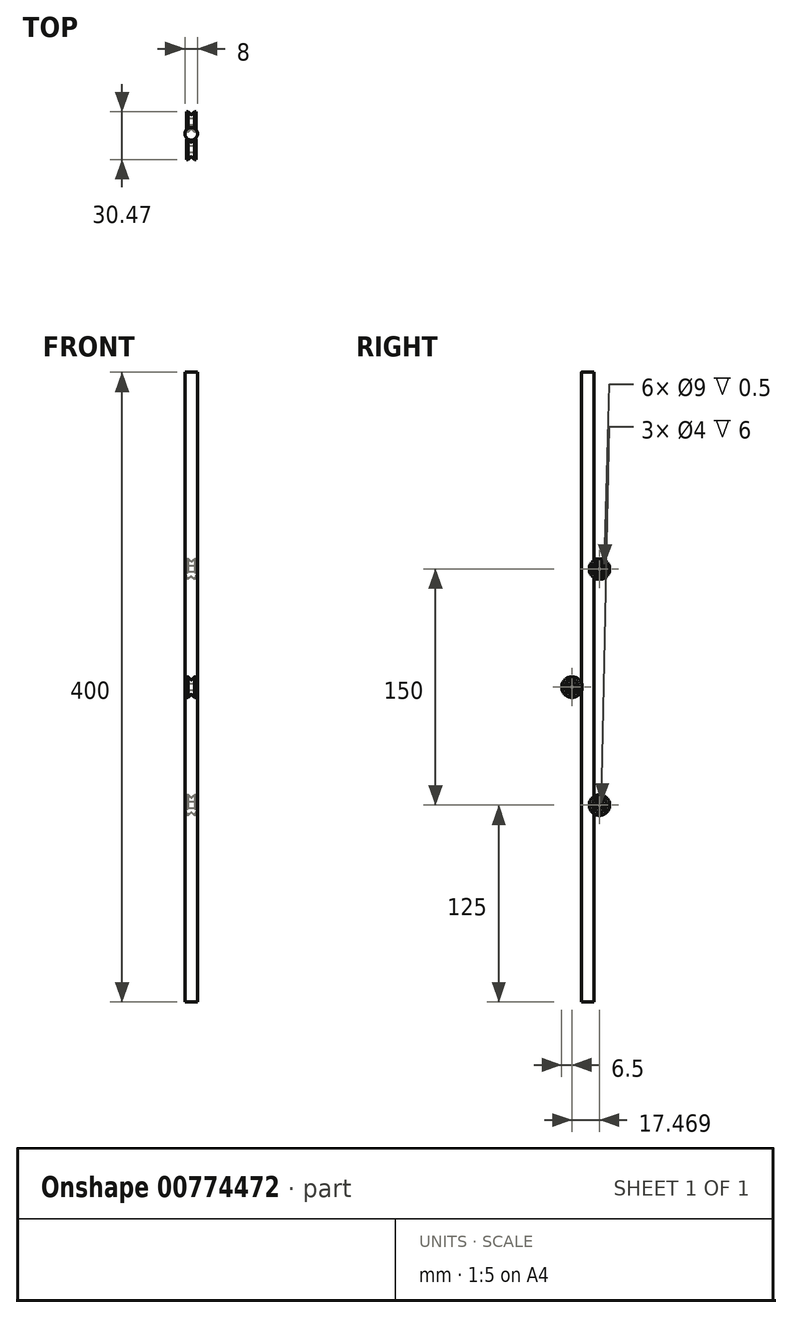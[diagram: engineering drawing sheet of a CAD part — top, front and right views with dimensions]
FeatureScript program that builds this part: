
annotation { "Feature Type Name" : "Feature", "Feature Type Description" : "" }
export const myFeature = defineFeature(function(context is Context, id is Id, definition is map)
    precondition{}
    {
        {
            var Q0;
            Q0=qCreatedBy(makeId("Top.planeOp"),FACE);
            var sketch = newSketch(context, id + "F0", { "sketchPlane" : qUnion([Q0])});
            skLineSegment(sketch, "E0", {"start": v(0, -18.13) * mm, "end": v(0, 18.13) * mm, "construction": true});
            skLineSegment(sketch, "E1", {"start": v(-16.06, 0) * mm, "end": v(16.06, 0) * mm, "construction": true});
            skLineSegment(sketch, "E2", {"start": v(0.18, 4.68) * mm, "end": v(2, 6.5) * mm});
            skLineSegment(sketch, "E3", {"start": v(2, 6.5) * mm, "end": v(3, 6.5) * mm});
            skLineSegment(sketch, "E4", {"start": v(3, 2) * mm, "end": v(0, 2) * mm});
            skLineSegment(sketch, "E5", {"start": v(3, 2) * mm, "end": v(3, 2.5) * mm});
            skLineSegment(sketch, "E6", {"start": v(3, 2.5) * mm, "end": v(2.5, 2.5) * mm});
            skLineSegment(sketch, "E7", {"start": v(2.5, 2.5) * mm, "end": v(2.5, 4.5) * mm});
            skLineSegment(sketch, "E8", {"start": v(2.5, 4.5) * mm, "end": v(3, 4.5) * mm});
            skLineSegment(sketch, "E9", {"start": v(3, 4.5) * mm, "end": v(3, 6.5) * mm});
            skArc(sketch, "E10", {"start": v(0, 4.6) * mm, "mid": v(0.1, 4.62) * mm, "end": v(0.18, 4.68) * mm});
            skArc(sketch, "E11.MirrorCS", {"start": v(0, 4.6) * mm, "mid": v(-0.1, 4.62) * mm, "end": v(-0.18, 4.68) * mm});
            skLineSegment(sketch, "E12.MirrorCS", {"start": v(-3, 2.5) * mm, "end": v(-2.5, 2.5) * mm});
            skLineSegment(sketch, "E13.MirrorCS", {"start": v(-3, 2) * mm, "end": v(0, 2) * mm});
            skLineSegment(sketch, "E14.MirrorCS", {"start": v(-2.5, 2.5) * mm, "end": v(-2.5, 4.5) * mm});
            skLineSegment(sketch, "E15.MirrorCS", {"start": v(-2.5, 4.5) * mm, "end": v(-3, 4.5) * mm});
            skLineSegment(sketch, "E16.MirrorCS", {"start": v(-0.18, 4.68) * mm, "end": v(-2, 6.5) * mm});
            skLineSegment(sketch, "E17.MirrorCS", {"start": v(-3, 2) * mm, "end": v(-3, 2.5) * mm});
            skLineSegment(sketch, "E18.MirrorCS", {"start": v(-3, 4.5) * mm, "end": v(-3, 6.5) * mm});
            skLineSegment(sketch, "E19.MirrorCS", {"start": v(-2, 6.5) * mm, "end": v(-3, 6.5) * mm});
            skCircle(sketch, "E20", {"center": v(0, 9.96) * mm, "radius": 4 * mm});
            skLineSegment(sketch, "E21", {"start": v(3.56, 9.96) * mm, "end": v(8.79, 9.96) * mm, "construction": true});
            skLineSegment(sketch, "E22", {"start": v(4, 8.96) * mm, "end": v(12, 8.96) * mm});
            skLineSegment(sketch, "E23", {"start": v(12, 8.96) * mm, "end": v(12, 0.96) * mm});
            skLineSegment(sketch, "E24", {"start": v(12, 0.96) * mm, "end": v(14, 0.96) * mm});
            skLineSegment(sketch, "E25", {"start": v(14, 0.96) * mm, "end": v(14, 10.96) * mm});
            skLineSegment(sketch, "E26", {"start": v(14, 10.96) * mm, "end": v(4, 10.96) * mm});
            skLineSegment(sketch, "E27", {"start": v(4, 8.96) * mm, "end": v(4, 10.96) * mm});
            skSolve(sketch);
        }
        {
            var Q0;
            Q0=makeQuery(id+"F0.imprint","IMPRINT",FACE,{"disambiguationData":[TD([[makeQuery(id+"F0.imprint","IMPRINT",EDGE,{"derivedFrom":sQuery(id+"F0.wireOp",EDGE,"E2")}),-1.0]])]});
            var Q1;
            Q1=sQuery(id+"F0.wireOp",EDGE,"E1");
            revolve(context, id + "F1", {"surfaceOperationType" : NewSurfaceOperationType.NEW, "entities" : qUnion([Q0]), "axis" : qUnion([Q1]), "revolveType" : RevolveType.FULL});
        }
        {
            var Q0;
            {var subQ0=sQuery(id+"F0.wireOp",EDGE,"E20");var subQ1=makeQuery(id+"F0.imprint","INTERSECT",VERTEX,{"derivedFrom":[sQuery(id+"F0.wireOp",EDGE,"E2"),subQ0]});Q0=makeQuery(id+"F0.imprint","IMPRINT",FACE,{"disambiguationData":[TD([[makeQuery(id+"F0.imprint","IMPRINT",EDGE,{"disambiguationData":[TD([[subQ1,1.0]])],"derivedFrom":subQ0}),1.0]])]});}
            extrude(context, id + "F2", {"entities" : qUnion([Q0]), "endBound" : BoundingType.SYMMETRIC, "depth" : 400 * mm, "offsetDistance" : 25 * mm});
        }
        {
            var Q0;
            Q0=makeQuery(id+"F1.opRevolve","SWEPT_BODY",BODY,{"disambiguationData":[OSD([sQuery(id+"F0.wireOp",EDGE,"E2"),sQuery(id+"F0.wireOp",EDGE,"E3"),sQuery(id+"F0.wireOp",EDGE,"E4"),sQuery(id+"F0.wireOp",EDGE,"E5"),sQuery(id+"F0.wireOp",EDGE,"E6"),sQuery(id+"F0.wireOp",EDGE,"E7"),sQuery(id+"F0.wireOp",EDGE,"E8"),sQuery(id+"F0.wireOp",EDGE,"E9"),sQuery(id+"F0.wireOp",EDGE,"E10"),sQuery(id+"F0.wireOp",EDGE,"E11.MirrorCS"),sQuery(id+"F0.wireOp",EDGE,"E12.MirrorCS"),sQuery(id+"F0.wireOp",EDGE,"E13.MirrorCS"),sQuery(id+"F0.wireOp",EDGE,"E14.MirrorCS"),sQuery(id+"F0.wireOp",EDGE,"E15.MirrorCS"),sQuery(id+"F0.wireOp",EDGE,"E16.MirrorCS"),sQuery(id+"F0.wireOp",EDGE,"E17.MirrorCS"),sQuery(id+"F0.wireOp",EDGE,"E18.MirrorCS"),sQuery(id+"F0.wireOp",EDGE,"E19.MirrorCS")])]});
            transform(context, id + "F3", {"entities" : qUnion([Q0]), "transformType" : TransformType.TRANSLATION_3D, "dx" : 0 * mm, "dy" : 17.47 * mm, "dz" : 75 * mm, "makeCopy" : true});
        }
        {
            var Q0;
            Q0=makeQuery(id+"F3.opPattern","COPY",BODY,{"derivedFrom":makeQuery(id+"F1.opRevolve","SWEPT_BODY",BODY,{"disambiguationData":[OSD([sQuery(id+"F0.wireOp",EDGE,"E2"),sQuery(id+"F0.wireOp",EDGE,"E3"),sQuery(id+"F0.wireOp",EDGE,"E4"),sQuery(id+"F0.wireOp",EDGE,"E5"),sQuery(id+"F0.wireOp",EDGE,"E6"),sQuery(id+"F0.wireOp",EDGE,"E7"),sQuery(id+"F0.wireOp",EDGE,"E8"),sQuery(id+"F0.wireOp",EDGE,"E9"),sQuery(id+"F0.wireOp",EDGE,"E10"),sQuery(id+"F0.wireOp",EDGE,"E11.MirrorCS"),sQuery(id+"F0.wireOp",EDGE,"E12.MirrorCS"),sQuery(id+"F0.wireOp",EDGE,"E13.MirrorCS"),sQuery(id+"F0.wireOp",EDGE,"E14.MirrorCS"),sQuery(id+"F0.wireOp",EDGE,"E15.MirrorCS"),sQuery(id+"F0.wireOp",EDGE,"E16.MirrorCS"),sQuery(id+"F0.wireOp",EDGE,"E17.MirrorCS"),sQuery(id+"F0.wireOp",EDGE,"E18.MirrorCS"),sQuery(id+"F0.wireOp",EDGE,"E19.MirrorCS")])]}),"instanceName":"1"});
            transform(context, id + "F4", {"entities" : qUnion([Q0]), "transformType" : TransformType.TRANSLATION_3D, "dx" : 0 * mm, "dy" : 0 * mm, "dz" : -150 * mm, "makeCopy" : true});
        }
    });
